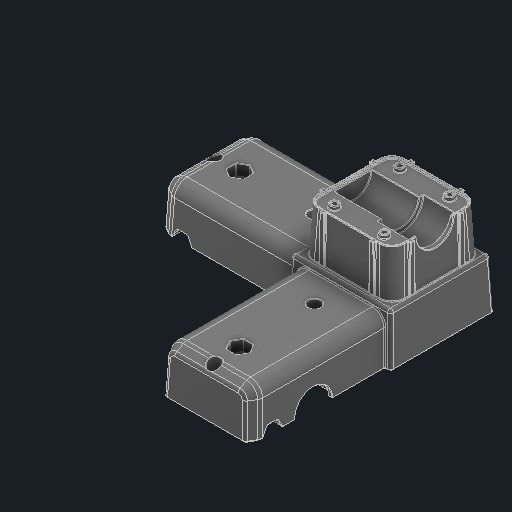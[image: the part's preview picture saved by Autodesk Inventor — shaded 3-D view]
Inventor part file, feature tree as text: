
AUTODESK INVENTOR PART (.ipt)
format: ipt  version: 2024.2 (Build 282272000, 272)  size: 7,264,256 bytes
history: native  units: in
note: dims shown in document units (in); Inventor stores cm internally (conversion verified against a paired STEP export)
features: fillet x1
ambient origin geometry x8: Origin, YZ Plane, XZ Plane, XY Plane, X Axis, Y Axis, Z Axis, Center Point
bodies: Solid1 (feature_tree)
feature tree (1):
  fillet  "Fillet107"  [1 undecoded]
note: 1 required parameter value undecoded (feature->parameter linkage not recoverable at this tier; creation-order binding heuristic only, values carry confidence <= 0.55)
